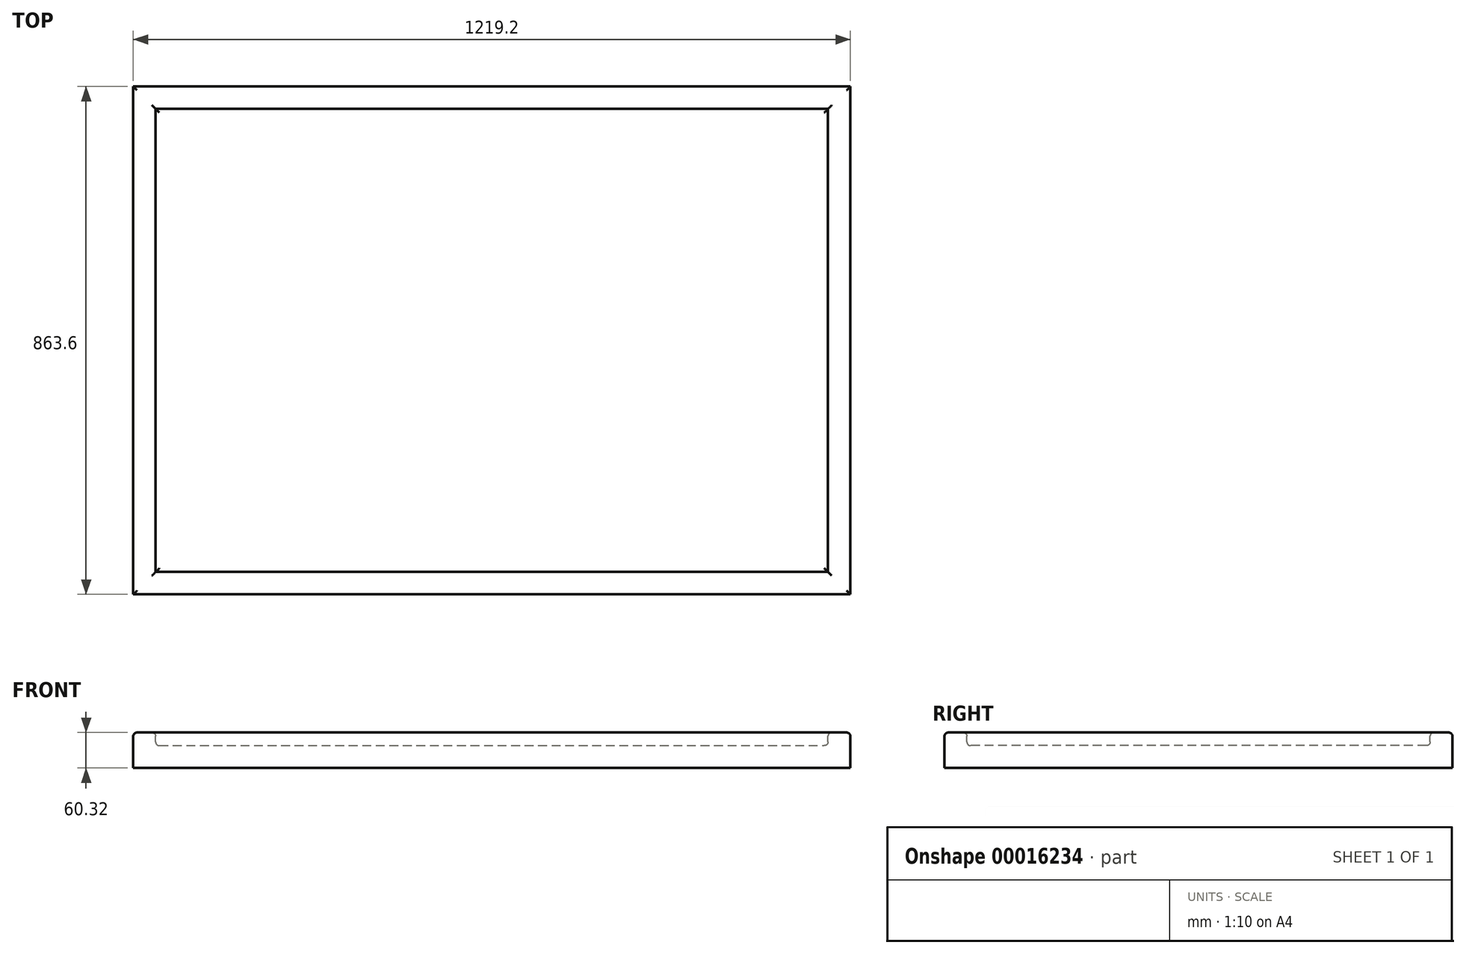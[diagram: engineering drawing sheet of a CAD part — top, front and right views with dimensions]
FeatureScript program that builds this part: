
annotation { "Feature Type Name" : "Feature", "Feature Type Description" : "" }
export const myFeature = defineFeature(function(context is Context, id is Id, definition is map)
    precondition{}
    {
        {
            var Q0;
            Q0=qCreatedBy(makeId("Top.planeOp"),FACE);
            var sketch = newSketch(context, id + "F0", { "sketchPlane" : qUnion([Q0])});
            skLineSegment(sketch, "E0.bottom", {"start": v(-770.1, -6.33) * mm, "end": v(449.1, -6.33) * mm});
            skLineSegment(sketch, "E0.top", {"start": v(-770.1, -869.93) * mm, "end": v(449.1, -869.93) * mm});
            skLineSegment(sketch, "E0.left", {"start": v(-770.1, -6.33) * mm, "end": v(-770.1, -869.93) * mm});
            skLineSegment(sketch, "E0.right", {"start": v(449.1, -6.33) * mm, "end": v(449.1, -869.93) * mm});
            skSolve(sketch);
        }
        {
            var Q0;
            Q0=makeQuery(id+"F0.imprint","IMPRINT",FACE,{"disambiguationData":[TD([[makeQuery(id+"F0.imprint","IMPRINT",EDGE,{"derivedFrom":sQuery(id+"F0.wireOp",EDGE,"E0.bottom")}),-1.0]])]});
            extrude(context, id + "F1", {"entities" : qUnion([Q0]), "oppositeDirection" : true, "depth" : 60.32 * mm});
        }
        {
            var Q0;
            Q0=makeQuery(id+"F1.opExtrude","CAP_FACE",FACE,{"disambiguationData":[OSD([sQuery(id+"F0.wireOp",EDGE,"E0.bottom"),sQuery(id+"F0.wireOp",EDGE,"E0.top"),sQuery(id+"F0.wireOp",EDGE,"E0.left"),sQuery(id+"F0.wireOp",EDGE,"E0.right")])],"isStart":true});
            shell(context, id + "F2", {"entities" : qUnion([Q0]), "thickness" : 38.1 * mm});
        }
        {
            var Q0;
            {var subQ0=sQuery(id+"F0.wireOp",EDGE,"E0.left");Q0=makeQuery(id+"F2.opShell","OFFSET_EDGE",EDGE,{"disambiguationData":[OSD([subQ0]),TDD([makeQuery(id+"F1.opExtrude","CAP_EDGE",EDGE,{"disambiguationData":[OSD([subQ0])],"isStart":true})])]});}
            var Q1;
            Q1=makeQuery(id+"F1.opExtrude","CAP_FACE",FACE,{"disambiguationData":[OSD([sQuery(id+"F0.wireOp",EDGE,"E0.bottom"),sQuery(id+"F0.wireOp",EDGE,"E0.top"),sQuery(id+"F0.wireOp",EDGE,"E0.left"),sQuery(id+"F0.wireOp",EDGE,"E0.right")])],"isStart":true});
            var Q2;
            {var subQ0=sQuery(id+"F0.wireOp",EDGE,"E0.bottom");Q2=makeQuery(id+"F2.opShell","OFFSET_EDGE",EDGE,{"disambiguationData":[OSD([subQ0]),TDD([makeQuery(id+"F1.opExtrude","CAP_EDGE",EDGE,{"disambiguationData":[OSD([subQ0])],"isStart":false})])]});}
            var Q3;
            {var subQ0=sQuery(id+"F0.wireOp",EDGE,"E0.left");Q3=makeQuery(id+"F2.opShell","OFFSET_EDGE",EDGE,{"disambiguationData":[OSD([subQ0]),TDD([makeQuery(id+"F1.opExtrude","CAP_EDGE",EDGE,{"disambiguationData":[OSD([subQ0])],"isStart":false})])]});}
            var Q4;
            {var subQ0=sQuery(id+"F0.wireOp",EDGE,"E0.right");Q4=makeQuery(id+"F2.opShell","OFFSET_EDGE",EDGE,{"disambiguationData":[OSD([subQ0]),TDD([makeQuery(id+"F1.opExtrude","CAP_EDGE",EDGE,{"disambiguationData":[OSD([subQ0])],"isStart":false})])]});}
            var Q5;
            {var subQ0=sQuery(id+"F0.wireOp",EDGE,"E0.top");Q5=makeQuery(id+"F2.opShell","OFFSET_EDGE",EDGE,{"disambiguationData":[OSD([subQ0]),TDD([makeQuery(id+"F1.opExtrude","CAP_EDGE",EDGE,{"disambiguationData":[OSD([subQ0])],"isStart":false})])]});}
            fillet(context, id + "F3", {"entities" : qUnion([Q0, Q1, Q2, Q3, Q4, Q5]), "radius" : 6.35 * mm, "tangentPropagation" : true, "allowEdgeOverflow" : false});
        }
    });
